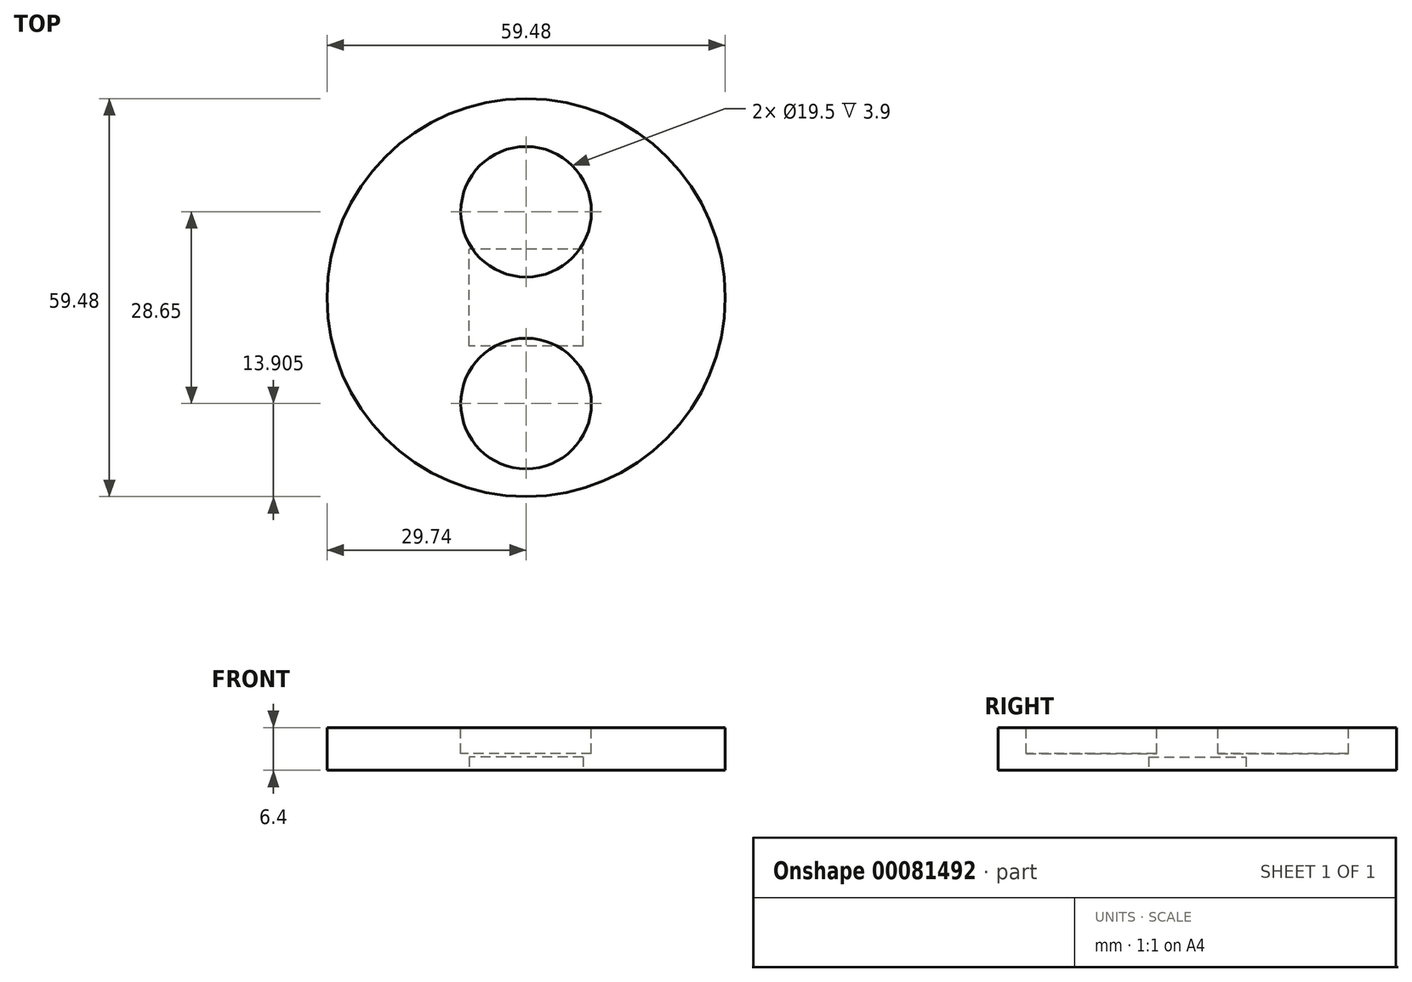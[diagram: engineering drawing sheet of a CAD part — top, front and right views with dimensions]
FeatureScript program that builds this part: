
annotation { "Feature Type Name" : "Feature", "Feature Type Description" : "" }
export const myFeature = defineFeature(function(context is Context, id is Id, definition is map)
    precondition{}
    {
        {
            var Q0;
            Q0=qCreatedBy(makeId("Top.planeOp"),FACE);
            var sketch = newSketch(context, id + "F0", { "sketchPlane" : qUnion([Q0])});
            skCircle(sketch, "E0", {"center": v(0, 0) * mm, "radius": 29.74 * mm});
            skSolve(sketch);
        }
        {
            var Q0;
            Q0 = qSketchRegion(id + "F0", true);
            extrude(context, id + "F1", {"entities" : qUnion([Q0]), "depth" : 6.4 * mm});
        }
        {
            var Q0;
            Q0=makeQuery(id+"F1.opExtrude","CAP_FACE",FACE,{"disambiguationData":[OSD([sQuery(id+"F0.wireOp",EDGE,"E0")])],"isStart":false});
            var sketch = newSketch(context, id + "F2", { "sketchPlane" : qUnion([Q0])});
            skCircle(sketch, "E1", {"center": v(0, 12.81) * mm, "radius": 9.75 * mm});
            skCircle(sketch, "E2", {"center": v(0, -15.84) * mm, "radius": 9.75 * mm});
            skSolve(sketch);
        }
        {
            var Q0;
            Q0 = qSketchRegion(id + "F2", true);
            extrude(context, id + "F3", {"entities" : qUnion([Q0]), "operationType" : NewBodyOperationType.REMOVE, "oppositeDirection" : true, "depth" : 3.9 * mm});
        }
        {
            var Q0;
            Q0=makeQuery(id+"F1.opExtrude","CAP_FACE",FACE,{"disambiguationData":[OSD([sQuery(id+"F0.wireOp",EDGE,"E0")])],"isStart":true});
            var sketch = newSketch(context, id + "F4", { "sketchPlane" : qUnion([Q0])});
            skLineSegment(sketch, "E3.bottom", {"start": v(8.5, 7.25) * mm, "end": v(-8.5, 7.25) * mm});
            skLineSegment(sketch, "E3.top", {"start": v(8.5, -7.25) * mm, "end": v(-8.5, -7.25) * mm});
            skLineSegment(sketch, "E3.left", {"start": v(8.5, 7.25) * mm, "end": v(8.5, -7.25) * mm});
            skLineSegment(sketch, "E3.right", {"start": v(-8.5, 7.25) * mm, "end": v(-8.5, -7.25) * mm});
            skPoint(sketch, "E3.middle", {"position": v(0, 0) * mm});
            skSolve(sketch);
        }
        {
            var Q0;
            Q0 = qSketchRegion(id + "F4", true);
            extrude(context, id + "F5", {"entities" : qUnion([Q0]), "operationType" : NewBodyOperationType.REMOVE, "oppositeDirection" : true, "depth" : 2 * mm});
        }
    });
